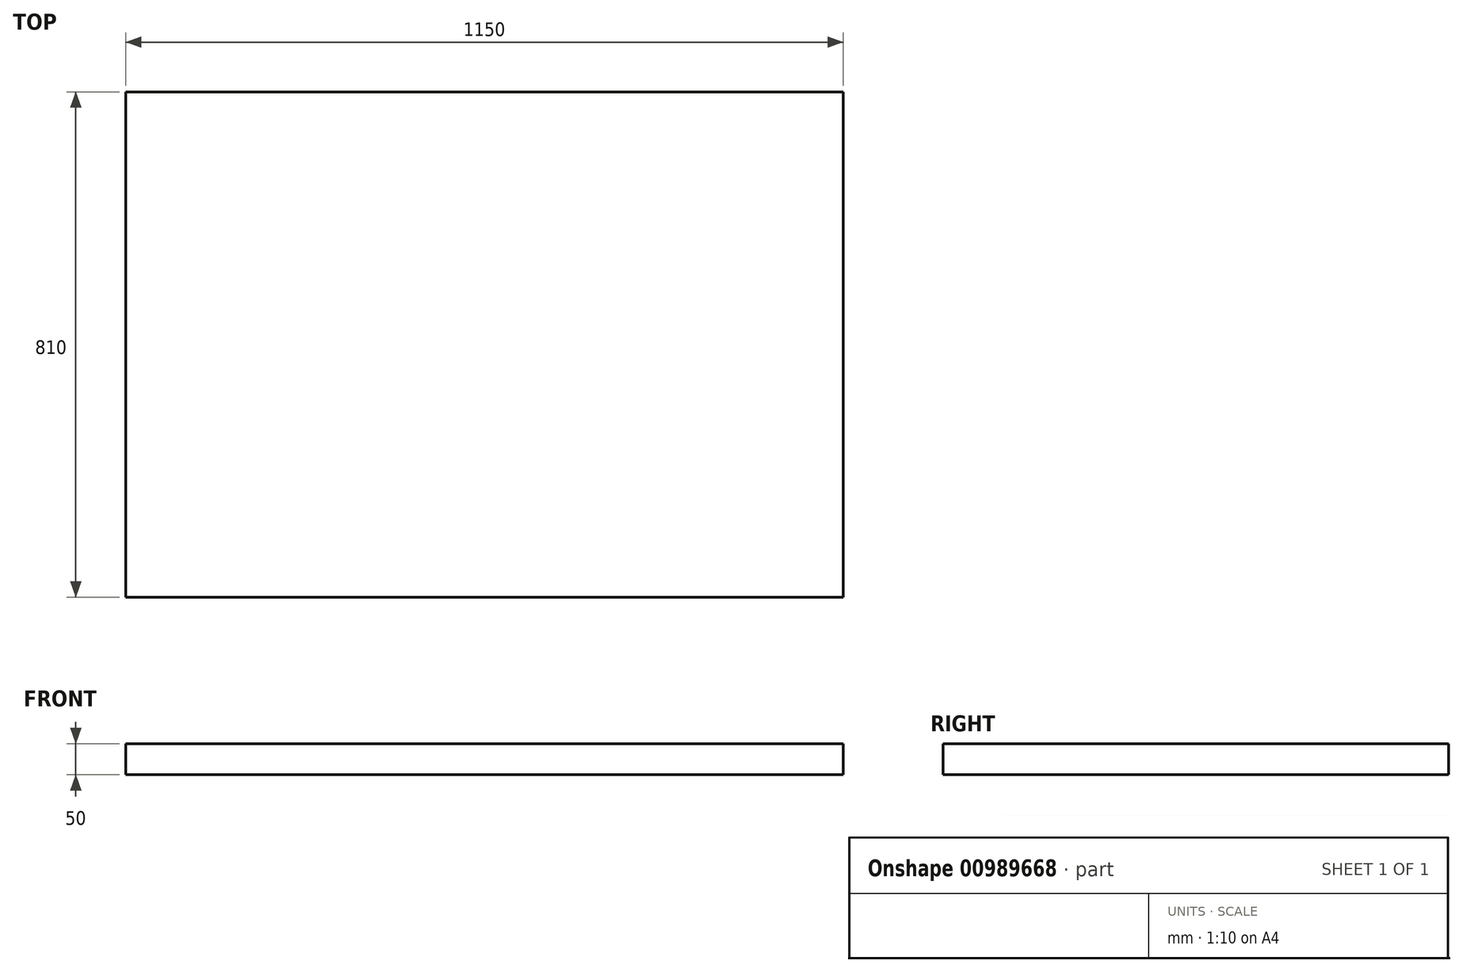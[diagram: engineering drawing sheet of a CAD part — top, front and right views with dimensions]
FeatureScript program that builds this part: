
annotation { "Feature Type Name" : "Feature", "Feature Type Description" : "" }
export const myFeature = defineFeature(function(context is Context, id is Id, definition is map)
    precondition{}
    {
        {
            var Q0;
            Q0=qCreatedBy(makeId("Top.planeOp"),FACE);
            var sketch = newSketch(context, id + "F0", { "sketchPlane" : qUnion([Q0])});
            skLineSegment(sketch, "E0.bottom", {"start": v(0, 0) * mm, "end": v(1150, 0) * mm});
            skLineSegment(sketch, "E0.top", {"start": v(0, 810) * mm, "end": v(1150, 810) * mm});
            skLineSegment(sketch, "E0.left", {"start": v(0, 0) * mm, "end": v(0, 810) * mm});
            skLineSegment(sketch, "E0.right", {"start": v(1150, 0) * mm, "end": v(1150, 810) * mm});
            skSolve(sketch);
        }
        {
            var Q0;
            Q0 = qSketchRegion(id + "F0", true);
            extrude(context, id + "F1", {"entities" : qUnion([Q0]), "depth" : 50 * mm, "offsetDistance" : 25 * mm});
        }
    });
